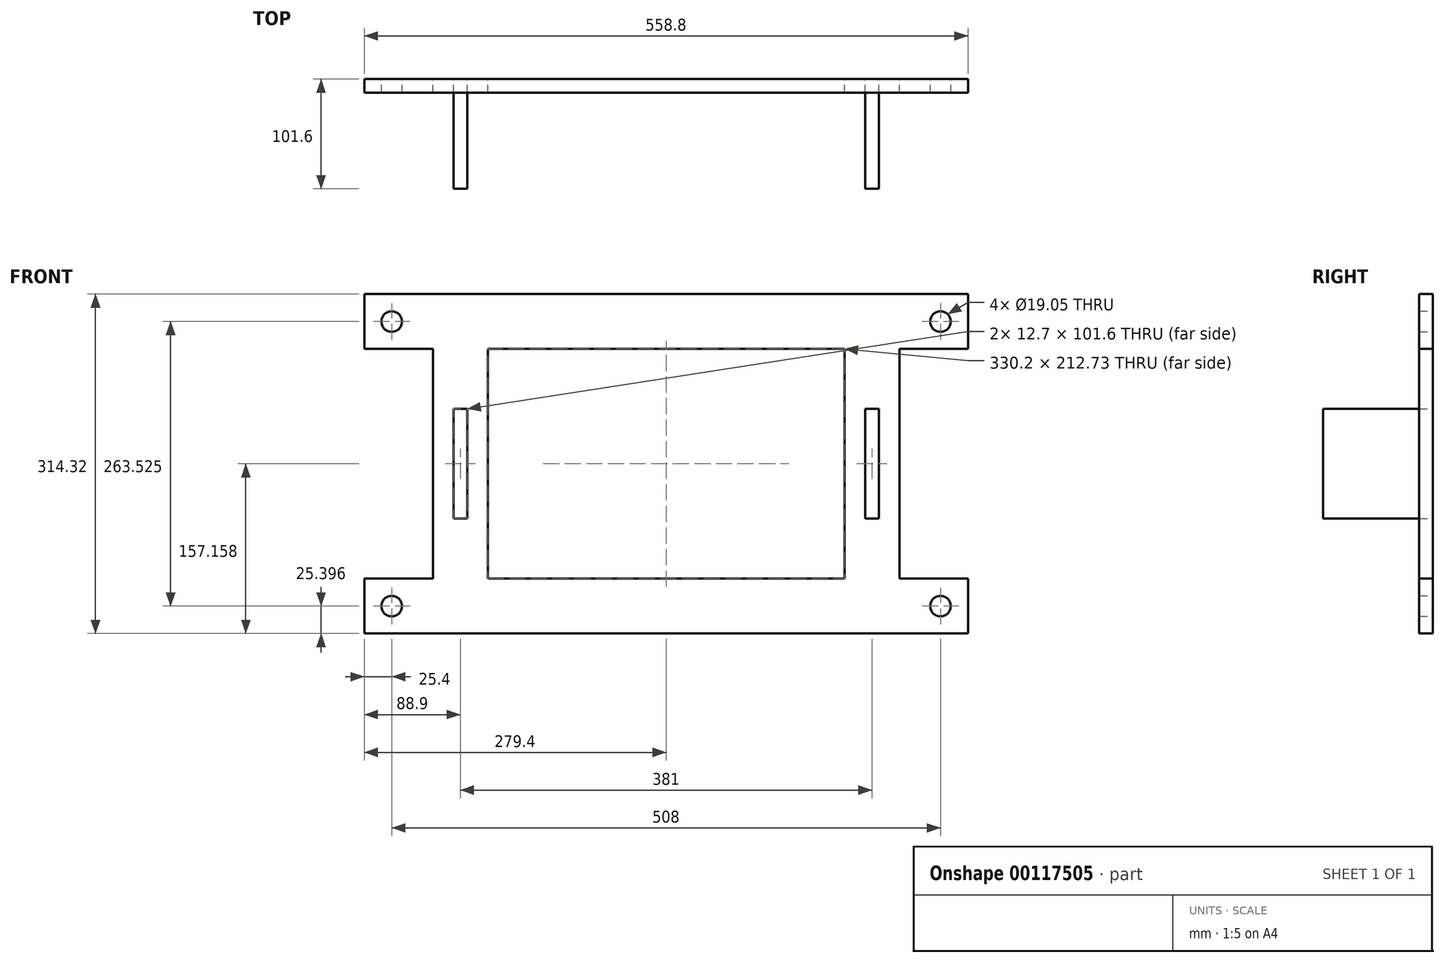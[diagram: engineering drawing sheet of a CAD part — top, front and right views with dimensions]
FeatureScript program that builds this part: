
annotation { "Feature Type Name" : "Feature", "Feature Type Description" : "" }
export const myFeature = defineFeature(function(context is Context, id is Id, definition is map)
    precondition{}
    {
        {
            var Q0;
            Q0=qCreatedBy(makeId("Front.planeOp"),FACE);
            var sketch = newSketch(context, id + "F0", { "sketchPlane" : qUnion([Q0])});
            skLineSegment(sketch, "E0.bottom", {"start": v(279.4, 50.51) * mm, "end": v(-279.4, 50.51) * mm});
            skLineSegment(sketch, "E0.top", {"start": v(279.4, 101.31) * mm, "end": v(-279.4, 101.31) * mm});
            skLineSegment(sketch, "E0.left", {"start": v(279.4, 50.51) * mm, "end": v(279.4, 101.31) * mm});
            skLineSegment(sketch, "E0.right", {"start": v(-279.4, 50.51) * mm, "end": v(-279.4, 101.31) * mm});
            skPoint(sketch, "E0.middle", {"position": v(0, 75.91) * mm});
            skLineSegment(sketch, "E1.bottom", {"start": v(279.4, -213.01) * mm, "end": v(-279.4, -213.01) * mm});
            skLineSegment(sketch, "E1.top", {"start": v(279.4, -162.21) * mm, "end": v(-279.4, -162.21) * mm});
            skLineSegment(sketch, "E1.left", {"start": v(279.4, -213.01) * mm, "end": v(279.4, -162.21) * mm});
            skLineSegment(sketch, "E1.right", {"start": v(-279.4, -213.01) * mm, "end": v(-279.4, -162.21) * mm});
            skPoint(sketch, "E1.middle", {"position": v(0, -187.61) * mm});
            skLineSegment(sketch, "E2.bottom", {"start": v(-215.9, 50.51) * mm, "end": v(-165.1, 50.51) * mm});
            skLineSegment(sketch, "E2.top", {"start": v(-215.9, -162.21) * mm, "end": v(-165.1, -162.21) * mm});
            skLineSegment(sketch, "E2.left", {"start": v(-215.9, 50.51) * mm, "end": v(-215.9, -162.21) * mm});
            skLineSegment(sketch, "E2.right", {"start": v(-165.1, 50.51) * mm, "end": v(-165.1, -162.21) * mm});
            skLineSegment(sketch, "E3.bottom", {"start": v(165.1, 50.51) * mm, "end": v(215.9, 50.51) * mm});
            skLineSegment(sketch, "E3.top", {"start": v(165.1, -162.21) * mm, "end": v(215.9, -162.21) * mm});
            skLineSegment(sketch, "E3.left", {"start": v(165.1, 50.51) * mm, "end": v(165.1, -162.21) * mm});
            skLineSegment(sketch, "E3.right", {"start": v(215.9, 50.51) * mm, "end": v(215.9, -162.21) * mm});
            skPoint(sketch, "E4", {"position": v(-190.5, -55.85) * mm});
            skPoint(sketch, "E4.positionSnap0", {"position": v(-165.1, -55.85) * mm});
            skPoint(sketch, "E4.positionSnap1", {"position": v(-190.5, 50.51) * mm});
            skPoint(sketch, "E5", {"position": v(190.5, -55.85) * mm});
            skPoint(sketch, "E5.positionSnap0", {"position": v(190.5, 50.51) * mm});
            skPoint(sketch, "E5.positionSnap1", {"position": v(165.1, -55.85) * mm});
            skPoint(sketch, "E6", {"position": v(-254, 75.91) * mm});
            skPoint(sketch, "E6.positionSnap0", {"position": v(-279.4, 75.91) * mm});
            skPoint(sketch, "E7", {"position": v(254, 75.91) * mm});
            skPoint(sketch, "E8", {"position": v(254, -187.61) * mm});
            skPoint(sketch, "E8.positionSnap0", {"position": v(279.4, -187.61) * mm});
            skPoint(sketch, "E9", {"position": v(-254, -187.61) * mm});
            skPoint(sketch, "E9.positionSnap0", {"position": v(-279.4, -187.61) * mm});
            skLineSegment(sketch, "E10.bottom", {"start": v(-184.15, -106.65) * mm, "end": v(-196.85, -106.65) * mm});
            skLineSegment(sketch, "E10.top", {"start": v(-184.15, -5.05) * mm, "end": v(-196.85, -5.05) * mm});
            skLineSegment(sketch, "E10.left", {"start": v(-184.15, -106.65) * mm, "end": v(-184.15, -5.05) * mm});
            skLineSegment(sketch, "E10.right", {"start": v(-196.85, -106.65) * mm, "end": v(-196.85, -5.05) * mm});
            skLineSegment(sketch, "E11.bottom", {"start": v(196.85, -106.65) * mm, "end": v(184.15, -106.65) * mm});
            skLineSegment(sketch, "E11.top", {"start": v(196.85, -5.05) * mm, "end": v(184.15, -5.05) * mm});
            skLineSegment(sketch, "E11.left", {"start": v(196.85, -106.65) * mm, "end": v(196.85, -5.05) * mm});
            skLineSegment(sketch, "E11.right", {"start": v(184.15, -106.65) * mm, "end": v(184.15, -5.05) * mm});
            skSolve(sketch);
        }
        {
            var Q0;
            Q0 = qSketchRegion(id + "F0", true);
            extrude(context, id + "F1", {"entities" : qUnion([Q0]), "depth" : 12.7 * mm});
        }
        {
            var Q0;
            Q0=sQuery(id+"F0.wireOp",VERTEX,"E6");
            var Q1;
            Q1=sQuery(id+"F0.wireOp",VERTEX,"E7");
            var Q2;
            Q2=sQuery(id+"F0.wireOp",VERTEX,"E8");
            var Q3;
            Q3=sQuery(id+"F0.wireOp",VERTEX,"E9");
            var Q4;
            Q4=makeQuery(id+"F1.opExtrude","SWEPT_BODY",BODY,{"disambiguationData":[OSD([sQuery(id+"F0.wireOp",EDGE,"E0.bottom"),sQuery(id+"F0.wireOp",EDGE,"E0.top"),sQuery(id+"F0.wireOp",EDGE,"E0.left"),sQuery(id+"F0.wireOp",EDGE,"E0.right"),sQuery(id+"F0.wireOp",EDGE,"E1.bottom"),sQuery(id+"F0.wireOp",EDGE,"E1.top"),sQuery(id+"F0.wireOp",EDGE,"E1.left"),sQuery(id+"F0.wireOp",EDGE,"E1.right"),sQuery(id+"F0.wireOp",EDGE,"E2.left"),sQuery(id+"F0.wireOp",EDGE,"E2.right"),sQuery(id+"F0.wireOp",EDGE,"E3.left"),sQuery(id+"F0.wireOp",EDGE,"E3.right")])]});
            hole(context, id + "F2", {"style" : HoleStyle.SIMPLE, "endStyle" : HoleEndStyle.THROUGH, "oppositeDirection" : true, "holeDiameter" : 19.05 * mm, "locations" : qUnion([Q0, Q1, Q2, Q3]), "scope" : qUnion([Q4]), "isTappedThrough" : true});
        }
        {
            var Q0;
            Q0=makeQuery(id+"F0.imprint","IMPRINT",FACE,{"disambiguationData":[TD([[makeQuery(id+"F0.imprint","IMPRINT",EDGE,{"derivedFrom":sQuery(id+"F0.wireOp",EDGE,"E11.bottom")}),-1.0]])]});
            var Q1;
            Q1=makeQuery(id+"F0.imprint","IMPRINT",FACE,{"disambiguationData":[TD([[makeQuery(id+"F0.imprint","IMPRINT",EDGE,{"derivedFrom":sQuery(id+"F0.wireOp",EDGE,"E10.bottom")}),-1.0]])]});
            extrude(context, id + "F3", {"entities" : qUnion([Q0, Q1]), "depth" : 101.6 * mm});
        }
    });
